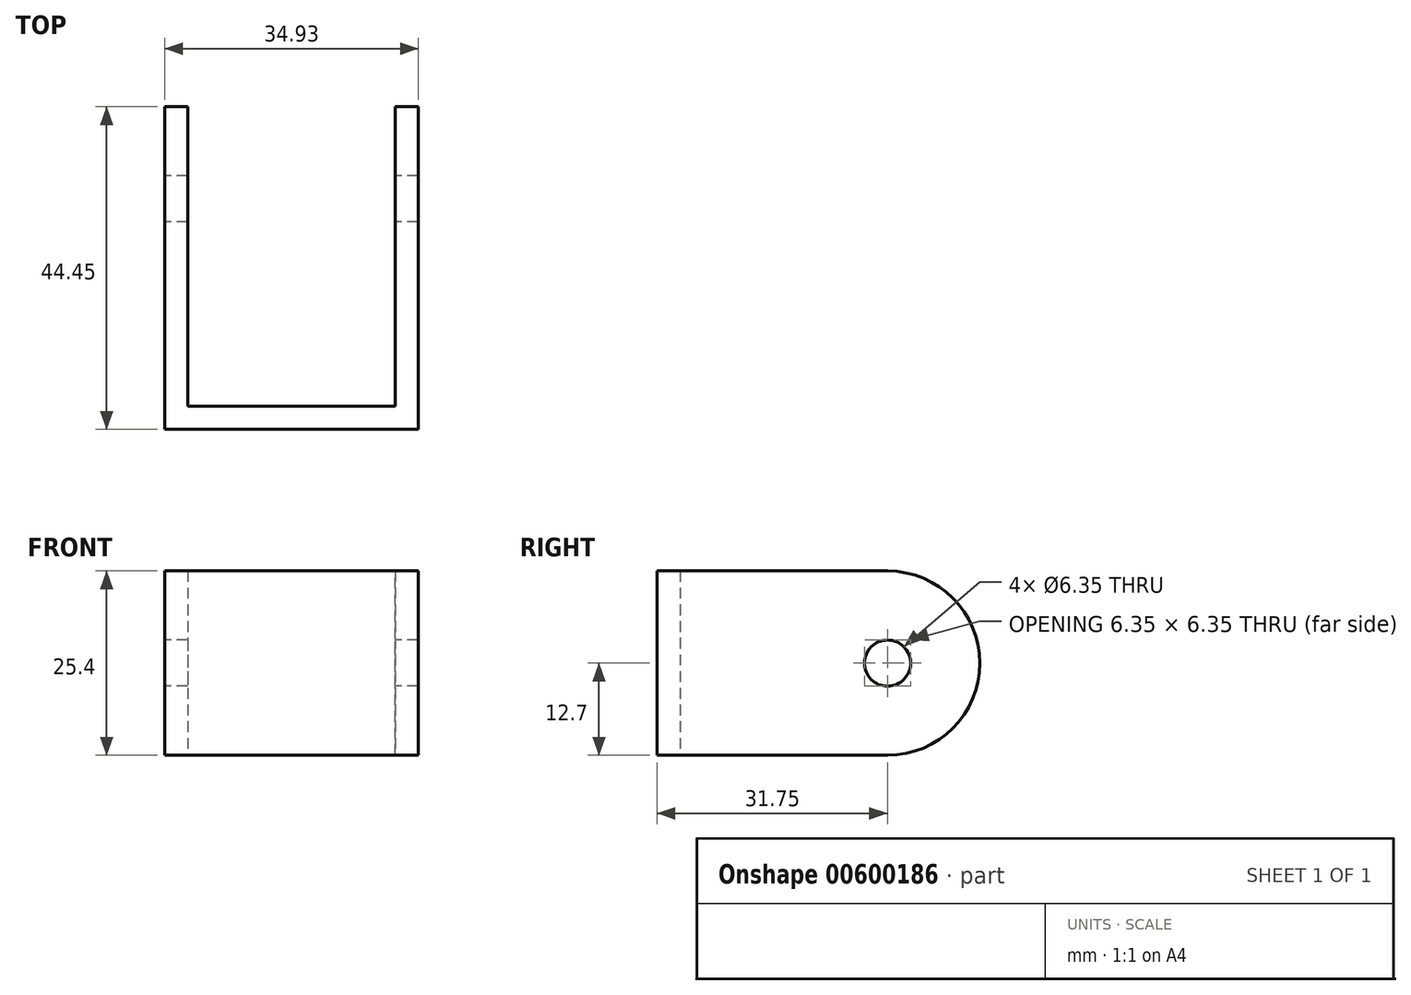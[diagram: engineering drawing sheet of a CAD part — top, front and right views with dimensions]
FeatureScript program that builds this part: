
annotation { "Feature Type Name" : "Feature", "Feature Type Description" : "" }
export const myFeature = defineFeature(function(context is Context, id is Id, definition is map)
    precondition{}
    {
        {
            var Q0;
            Q0=qCreatedBy(makeId("Top.planeOp"),FACE);
            var sketch = newSketch(context, id + "F0", { "sketchPlane" : qUnion([Q0])});
            skLineSegment(sketch, "E0", {"start": v(0, 0) * mm, "end": v(0, -44.45) * mm});
            skLineSegment(sketch, "E1", {"start": v(0, -44.45) * mm, "end": v(34.92, -44.45) * mm});
            skLineSegment(sketch, "E2", {"start": v(34.92, -44.45) * mm, "end": v(34.92, 0) * mm});
            skLineSegment(sketch, "E3", {"start": v(34.92, 0) * mm, "end": v(31.75, 0) * mm});
            skLineSegment(sketch, "E4", {"start": v(31.75, 0) * mm, "end": v(31.75, -41.28) * mm});
            skLineSegment(sketch, "E5", {"start": v(31.75, -41.27) * mm, "end": v(3.18, -41.28) * mm});
            skLineSegment(sketch, "E6", {"start": v(3.18, -41.28) * mm, "end": v(3.18, 0) * mm});
            skLineSegment(sketch, "E7", {"start": v(3.18, 0) * mm, "end": v(0, 0) * mm});
            skSolve(sketch);
        }
        {
            var Q0;
            Q0 = qSketchRegion(id + "F0", true);
            extrude(context, id + "F1", {"entities" : qUnion([Q0]), "depth" : 25.4 * mm, "offsetDistance" : 25.4 * mm});
        }
        {
            var Q0;
            Q0=qCreatedBy(makeId("Right.planeOp"),FACE);
            var sketch = newSketch(context, id + "F2", { "sketchPlane" : qUnion([Q0])});
            skLineSegment(sketch, "E8.left", {"start": v(0, 12.7) * mm, "end": v(0, 12.7) * mm});
            skPoint(sketch, "E9.visualSharp", {"position": v(0, 25.4) * mm});
            skArc(sketch, "E9.filletArc", {"start": v(0, 12.7) * mm, "mid": v(-3.72, 21.68) * mm, "end": v(-12.7, 25.4) * mm});
            skPoint(sketch, "E10.visualSharp", {"position": v(0, 0) * mm});
            skArc(sketch, "E10.filletArc", {"start": v(-12.7, 0) * mm, "mid": v(-3.72, 3.72) * mm, "end": v(0, 12.7) * mm});
            skLineSegment(sketch, "E11", {"start": v(-12.7, 25.4) * mm, "end": v(0, 25.4) * mm});
            skLineSegment(sketch, "E12", {"start": v(0, 0) * mm, "end": v(-12.7, 0) * mm});
            skPoint(sketch, "E8.right.end.orphan", {"position": v(-44.45, 25.4) * mm});
            skLineSegment(sketch, "E13", {"start": v(0, 25.4) * mm, "end": v(0, 0) * mm});
            skCircle(sketch, "E14", {"center": v(-12.7, 12.7) * mm, "radius": 3.18 * mm});
            skSolve(sketch);
        }
        {
            var Q0;
            Q0 = qSketchRegion(id + "F2", true);
            extrude(context, id + "F3", {"entities" : qUnion([Q0]), "operationType" : NewBodyOperationType.REMOVE, "depth" : 34.92 * mm, "offsetDistance" : 25.4 * mm});
        }
    });
